# Revit family: AD-C.SAT
name_source: partatom
category: Communication Devices
revit_build: Autodesk Revit 2015 (Build: 20160512_0715(x64)
units: mm (PartAtom-declared; Revit-internal decimal feet)

## types (1)
- AD-C.SAT
    Coverage Horizontal = 170.00°
    Coverage Vertical = 170.00°
    Default Elevation = 0 mm
    Depth = 86 mm
    Description = 2.75-inch small format ceiling satellite loudspeaker
    Enclosure Depth = 73.6 mm
    Enclosure Radius = 55.5 mm
    Grille Depth = 4.9 mm
    Grille Radius Base = 75 mm
    Grille Radius Extent = 53.8 mm
    Impedance = 16
    Manufacturer = QSC
    Manufacturer URL = www.qsc.com
    Middle Depth = 7.5 mm
    Middle Radius = 55.5 mm
    Model = AD-C.SAT
    Power Handling = 25
    Product Documentation Link = https://www.qsc.com
    Product Page URL = https://www.qsc.com
    Regulatory Compliance = UL1480, UL2043, NFPA90, NFPA70 suitable for use in air handling spaces.
Transformer UL registered per UL1876, ROHS, CE compliant. 
Baffle meets UL94-V0 and UL94-5VB flamibility rating; in accordance with 
IEC60849 / EN60849 systems
    SPL Max = 96
    Sensitivity = 82
    URL = https://www.qsc.com
    Weight Product (kg) = 0.63
    Weight Product (lb) = 1.39
    Width = 150 mm

## geometry (parser evidence)
native form markers: Blend x11, Sweep x2
no freeform markers — native parametric forms only
